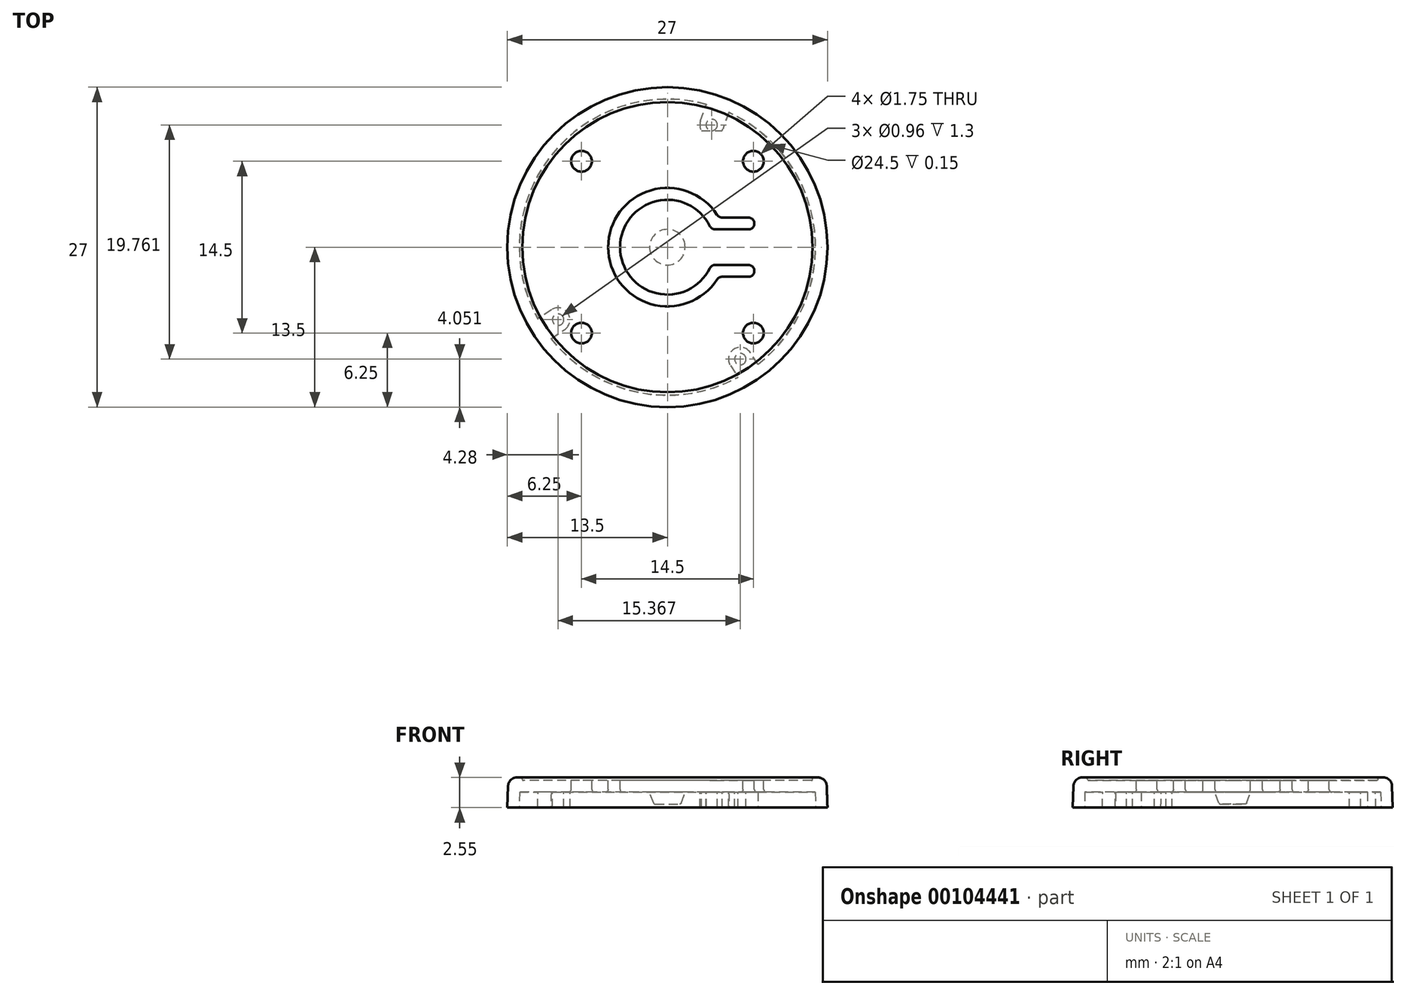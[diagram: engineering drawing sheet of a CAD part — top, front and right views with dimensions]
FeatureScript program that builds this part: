
annotation { "Feature Type Name" : "Feature", "Feature Type Description" : "" }
export const myFeature = defineFeature(function(context is Context, id is Id, definition is map)
    precondition{}
    {
        {
            var Q0;
            Q0=qCreatedBy(makeId("Top.planeOp"),FACE);
            var sketch = newSketch(context, id + "F0", { "sketchPlane" : qUnion([Q0])});
            skCircle(sketch, "E0", {"center": v(0, 0) * mm, "radius": 12.5 * mm});
            skCircle(sketch, "E1.0", {"center": v(0, 0) * mm, "radius": 13.5 * mm});
            skSolve(sketch);
        }
        {
            var Q0;
            Q0=qSketchRegion(id+"F0",true);
            var Q1;
            Q1=makeQuery(id+"F0.imprint","IMPRINT",FACE,{"disambiguationData":[TD([[makeQuery(id+"F0.imprint","IMPRINT",EDGE,{"derivedFrom":sQuery(id+"F0.wireOp",EDGE,"E0")}),1.0]])]});
            extrude(context, id + "F1", {"entities" : qUnion([Q0, Q1]), "depth" : 2.55 * mm, "hasDraft" : true, "draftAngle" : 2 * degree, "draftPullDirection" : true});
        }
        {
            var Q0;
            Q0=makeQuery(id+"F0.imprint","IMPRINT",FACE,{"disambiguationData":[TD([[makeQuery(id+"F0.imprint","IMPRINT",EDGE,{"derivedFrom":sQuery(id+"F0.wireOp",EDGE,"E0")}),1.0]])]});
            extrude(context, id + "F2", {"entities" : qUnion([Q0]), "operationType" : NewBodyOperationType.REMOVE, "depth" : 1.3 * mm, "hasDraft" : true, "draftAngle" : 1 * degree, "draftPullDirection" : true});
        }
        {
            var Q0;
            Q0=makeQuery(id+"F1.opExtrude","CAP_EDGE",EDGE,{"disambiguationData":[OSD([sQuery(id+"F0.wireOp",EDGE,"E1.0")])],"isStart":false});
            fillet(context, id + "F3", {"entities" : qUnion([Q0]), "radius" : .75 * mm, "tangentPropagation" : true, "allowEdgeOverflow" : false});
        }
        {
            var Q0;
            Q0=makeQuery(id+"F1.opExtrude","CAP_FACE",FACE,{"disambiguationData":[OSD([sQuery(id+"F0.wireOp",EDGE,"E1.0")])],"isStart":false});
            var sketch = newSketch(context, id + "F4", { "sketchPlane" : qUnion([Q0])});
            skCircle(sketch, "E2", {"center": v(0, 0) * mm, "radius": 12.25 * mm});
            skSolve(sketch);
        }
        {
            var Q0;
            Q0=qSketchRegion(id+"F4",true);
            extrude(context, id + "F5", {"entities" : qUnion([Q0]), "operationType" : NewBodyOperationType.REMOVE, "oppositeDirection" : true, "depth" : .25 * mm});
        }
        {
            var Q0;
            Q0=makeQuery(id+"F5.boolean.opBoolean","COPY",EDGE,{"derivedFrom":makeQuery(id+"F5.opExtrude","CAP_EDGE",EDGE,{"disambiguationData":[OSD([sQuery(id+"F4.wireOp",EDGE,"E2")])],"isStart":false})});
            var Q1;
            Q1=makeQuery(id+"F5.boolean.opBoolean","COPY",EDGE,{"derivedFrom":makeQuery(id+"F5.opExtrude","CAP_EDGE",EDGE,{"disambiguationData":[OSD([sQuery(id+"F4.wireOp",EDGE,"E2")])],"isStart":true})});
            fillet(context, id + "F6", {"entities" : qUnion([Q0, Q1]), "radius" : .1 * mm, "tangentPropagation" : true, "allowEdgeOverflow" : false});
        }
        {
            var Q0;
            Q0=makeQuery(id+"F5.boolean.opBoolean","COPY",FACE,{"derivedFrom":makeQuery(id+"F5.opExtrude","CAP_FACE",FACE,{"disambiguationData":[OSD([sQuery(id+"F4.wireOp",EDGE,"E2")])],"isStart":false})});
            var sketch = newSketch(context, id + "F7", { "sketchPlane" : qUnion([Q0])});
            skArc(sketch, "E3", {"start": v(3.58, 1.78) * mm, "mid": v(-4, 0) * mm, "end": v(3.58, -1.78) * mm});
            skLineSegment(sketch, "E4", {"start": v(0, 0) * mm, "end": v(11.07, 0) * mm, "construction": true});
            skLineSegment(sketch, "E5", {"start": v(4.03, 1.5) * mm, "end": v(6.83, 1.5) * mm});
            skLineSegment(sketch, "E6", {"start": v(7.33, 2) * mm, "end": v(7.33, 2) * mm});
            skLineSegment(sketch, "E7", {"start": v(6.83, 2.5) * mm, "end": v(4.6, 2.5) * mm});
            skLineSegment(sketch, "E8.0.MirrorCS", {"start": v(4.03, -1.5) * mm, "end": v(6.83, -1.5) * mm});
            skLineSegment(sketch, "E8.1.MirrorCS", {"start": v(6.83, -2.5) * mm, "end": v(4.6, -2.5) * mm});
            skLineSegment(sketch, "E8.2.MirrorCS", {"start": v(7.33, -2) * mm, "end": v(7.33, -2) * mm});
            skArc(sketch, "E9.trimOffspring", {"start": v(4.2, 2.73) * mm, "mid": v(-5, 0) * mm, "end": v(4.2, -2.73) * mm});
            skPoint(sketch, "E10.visualSharp", {"position": v(3.7, 1.5) * mm});
            skArc(sketch, "E10.filletArc", {"start": v(3.58, 1.78) * mm, "mid": v(3.77, 1.58) * mm, "end": v(4.03, 1.5) * mm});
            skPoint(sketch, "E11.visualSharp", {"position": v(4.33, 2.5) * mm});
            skArc(sketch, "E11.filletArc", {"start": v(4.2, 2.73) * mm, "mid": v(4.37, 2.56) * mm, "end": v(4.6, 2.5) * mm});
            skPoint(sketch, "E12.visualSharp", {"position": v(7.33, 2.5) * mm});
            skArc(sketch, "E12.filletArc", {"start": v(7.33, 2) * mm, "mid": v(7.18, 2.35) * mm, "end": v(6.83, 2.5) * mm});
            skPoint(sketch, "E13.visualSharp", {"position": v(7.33, 1.5) * mm});
            skArc(sketch, "E13.filletArc", {"start": v(6.83, 1.5) * mm, "mid": v(7.18, 1.65) * mm, "end": v(7.33, 2) * mm});
            skPoint(sketch, "E14.visualSharp", {"position": v(7.33, -1.5) * mm});
            skArc(sketch, "E14.filletArc", {"start": v(7.33, -2) * mm, "mid": v(7.18, -1.65) * mm, "end": v(6.83, -1.5) * mm});
            skPoint(sketch, "E15.visualSharp", {"position": v(7.33, -2.5) * mm});
            skArc(sketch, "E15.filletArc", {"start": v(6.83, -2.5) * mm, "mid": v(7.18, -2.35) * mm, "end": v(7.33, -2) * mm});
            skPoint(sketch, "E16.visualSharp", {"position": v(4.33, -2.5) * mm});
            skArc(sketch, "E16.filletArc", {"start": v(4.6, -2.5) * mm, "mid": v(4.37, -2.56) * mm, "end": v(4.2, -2.73) * mm});
            skPoint(sketch, "E17.visualSharp", {"position": v(3.7, -1.5) * mm});
            skArc(sketch, "E17.filletArc", {"start": v(4.03, -1.5) * mm, "mid": v(3.77, -1.58) * mm, "end": v(3.58, -1.78) * mm});
            skSolve(sketch);
        }
        {
            var Q0;
            Q0=qSketchRegion(id+"F7",true);
            extrude(context, id + "F8", {"entities" : qUnion([Q0]), "operationType" : NewBodyOperationType.REMOVE, "endBound" : BoundingType.THROUGH_ALL, "oppositeDirection" : true, "depth" : 25 * mm});
        }
        {
            var Q0;
            Q0=makeQuery(id+"F8.boolean.opBoolean","COPY",EDGE,{"derivedFrom":makeQuery(id+"F8.opExtrude","CAP_EDGE",EDGE,{"disambiguationData":[OSD([sQuery(id+"F7.wireOp",EDGE,"E9.trimOffspring")])],"isStart":true})});
            var Q1;
            Q1=makeQuery(id+"F8.boolean.opBoolean","INTERSECT",EDGE,{"derivedFrom":[makeQuery(id+"F2.boolean.opBoolean","COPY",FACE,{"derivedFrom":makeQuery(id+"F2.opExtrude","CAP_FACE",FACE,{"disambiguationData":[OSD([sQuery(id+"F0.wireOp",EDGE,"E0")])],"isStart":false})}),makeQuery(id+"F8.opExtrude","SWEPT_FACE",FACE,{"disambiguationData":[OSD([sQuery(id+"F7.wireOp",EDGE,"E9.trimOffspring")])]})]});
            fillet(context, id + "F9", {"entities" : qUnion([Q0, Q1]), "radius" : .25 * mm, "tangentPropagation" : true, "allowEdgeOverflow" : false});
        }
        {
            var Q0;
            Q0=makeQuery(id+"F2.boolean.opBoolean","COPY",FACE,{"derivedFrom":makeQuery(id+"F2.opExtrude","CAP_FACE",FACE,{"disambiguationData":[OSD([sQuery(id+"F0.wireOp",EDGE,"E0")])],"isStart":false})});
            var sketch = newSketch(context, id + "F10", { "sketchPlane" : qUnion([Q0])});
            skCircle(sketch, "E18", {"center": v(0, 0) * mm, "radius": 1.5 * mm});
            skSolve(sketch);
        }
        {
            var Q0;
            Q0=qSketchRegion(id+"F10",true);
            extrude(context, id + "F11", {"entities" : qUnion([Q0]), "operationType" : NewBodyOperationType.ADD, "depth" : 1 * mm, "hasDraft" : true, "draftAngle" : 20 * degree, "draftPullDirection" : true});
        }
        {
            var Q0;
            Q0=makeQuery(id+"F11.opExtrude","CAP_EDGE",EDGE,{"disambiguationData":[OSD([sQuery(id+"F10.wireOp",EDGE,"E18")])],"isStart":false});
            var Q1;
            Q1=makeQuery(id+"F11.opExtrude","CAP_EDGE",EDGE,{"disambiguationData":[OSD([sQuery(id+"F10.wireOp",EDGE,"E18")])],"isStart":true});
            fillet(context, id + "F12", {"entities" : qUnion([Q0, Q1]), "radius" : .15 * mm, "tangentPropagation" : true, "allowEdgeOverflow" : false});
        }
        {
            var Q0;
            Q0=makeQuery(id+"F5.boolean.opBoolean","COPY",FACE,{"derivedFrom":makeQuery(id+"F5.opExtrude","CAP_FACE",FACE,{"disambiguationData":[OSD([sQuery(id+"F4.wireOp",EDGE,"E2")])],"isStart":false})});
            var sketch = newSketch(context, id + "F13", { "sketchPlane" : qUnion([Q0])});
            skPoint(sketch, "E19.center", {"position": v(0, 0) * mm});
            skLineSegment(sketch, "E20", {"start": v(0, 0) * mm, "end": v(0, 14.83) * mm, "construction": true});
            skCircle(sketch, "E21", {"center": v(-7.25, 7.25) * mm, "radius": 0.88 * mm});
            skCircle(sketch, "E22.1.0", {"center": v(-7.25, -7.25) * mm, "radius": 0.88 * mm});
            skCircle(sketch, "E22.2.0", {"center": v(7.25, -7.25) * mm, "radius": 0.88 * mm});
            skCircle(sketch, "E22.3.0", {"center": v(7.25, 7.25) * mm, "radius": 0.88 * mm});
            skSolve(sketch);
        }
        {
            var Q0;
            Q0=qSketchRegion(id+"F13",true);
            extrude(context, id + "F14", {"entities" : qUnion([Q0]), "operationType" : NewBodyOperationType.REMOVE, "endBound" : BoundingType.THROUGH_ALL, "oppositeDirection" : true, "depth" : 25 * mm});
        }
        {
            var Q0;
            Q0=makeQuery(id+"F14.boolean.opBoolean","COPY",EDGE,{"derivedFrom":makeQuery(id+"F14.opExtrude","CAP_EDGE",EDGE,{"disambiguationData":[OSD([sQuery(id+"F13.wireOp",EDGE,"E21")])],"isStart":true})});
            var Q1;
            Q1=makeQuery(id+"F14.boolean.opBoolean","COPY",EDGE,{"derivedFrom":makeQuery(id+"F14.opExtrude","CAP_EDGE",EDGE,{"disambiguationData":[OSD([sQuery(id+"F13.wireOp",EDGE,"E22.3.0")])],"isStart":true})});
            var Q2;
            Q2=makeQuery(id+"F14.boolean.opBoolean","COPY",EDGE,{"derivedFrom":makeQuery(id+"F14.opExtrude","CAP_EDGE",EDGE,{"disambiguationData":[OSD([sQuery(id+"F13.wireOp",EDGE,"E22.2.0")])],"isStart":true})});
            var Q3;
            Q3=makeQuery(id+"F14.boolean.opBoolean","COPY",EDGE,{"derivedFrom":makeQuery(id+"F14.opExtrude","CAP_EDGE",EDGE,{"disambiguationData":[OSD([sQuery(id+"F13.wireOp",EDGE,"E22.1.0")])],"isStart":true})});
            var Q4;
            Q4=makeQuery(id+"F14.boolean.opBoolean","INTERSECT",EDGE,{"derivedFrom":[makeQuery(id+"F2.boolean.opBoolean","COPY",FACE,{"derivedFrom":makeQuery(id+"F2.opExtrude","CAP_FACE",FACE,{"disambiguationData":[OSD([sQuery(id+"F0.wireOp",EDGE,"E0")])],"isStart":false})}),makeQuery(id+"F14.opExtrude","SWEPT_FACE",FACE,{"disambiguationData":[OSD([sQuery(id+"F13.wireOp",EDGE,"E22.1.0")])]})]});
            var Q5;
            Q5=makeQuery(id+"F14.boolean.opBoolean","INTERSECT",EDGE,{"derivedFrom":[makeQuery(id+"F2.boolean.opBoolean","COPY",FACE,{"derivedFrom":makeQuery(id+"F2.opExtrude","CAP_FACE",FACE,{"disambiguationData":[OSD([sQuery(id+"F0.wireOp",EDGE,"E0")])],"isStart":false})}),makeQuery(id+"F14.opExtrude","SWEPT_FACE",FACE,{"disambiguationData":[OSD([sQuery(id+"F13.wireOp",EDGE,"E21")])]})]});
            var Q6;
            Q6=makeQuery(id+"F14.boolean.opBoolean","INTERSECT",EDGE,{"derivedFrom":[makeQuery(id+"F2.boolean.opBoolean","COPY",FACE,{"derivedFrom":makeQuery(id+"F2.opExtrude","CAP_FACE",FACE,{"disambiguationData":[OSD([sQuery(id+"F0.wireOp",EDGE,"E0")])],"isStart":false})}),makeQuery(id+"F14.opExtrude","SWEPT_FACE",FACE,{"disambiguationData":[OSD([sQuery(id+"F13.wireOp",EDGE,"E22.3.0")])]})]});
            var Q7;
            Q7=makeQuery(id+"F14.boolean.opBoolean","INTERSECT",EDGE,{"derivedFrom":[makeQuery(id+"F2.boolean.opBoolean","COPY",FACE,{"derivedFrom":makeQuery(id+"F2.opExtrude","CAP_FACE",FACE,{"disambiguationData":[OSD([sQuery(id+"F0.wireOp",EDGE,"E0")])],"isStart":false})}),makeQuery(id+"F14.opExtrude","SWEPT_FACE",FACE,{"disambiguationData":[OSD([sQuery(id+"F13.wireOp",EDGE,"E22.2.0")])]})]});
            fillet(context, id + "F15", {"entities" : qUnion([Q0, Q1, Q2, Q3, Q4, Q5, Q6, Q7]), "radius" : .25 * mm, "tangentPropagation" : true, "allowEdgeOverflow" : false});
        }
        {
            var Q0;
            Q0=makeQuery(id+"F2.boolean.opBoolean","COPY",FACE,{"derivedFrom":makeQuery(id+"F2.opExtrude","CAP_FACE",FACE,{"disambiguationData":[OSD([sQuery(id+"F0.wireOp",EDGE,"E0")])],"isStart":false})});
            var sketch = newSketch(context, id + "F16", { "sketchPlane" : qUnion([Q0])});
            skLineSegment(sketch, "E23", {"start": v(0, 0) * mm, "end": v(6.15, 9.45) * mm, "construction": true});
            skLineSegment(sketch, "E24", {"start": v(0, 0) * mm, "end": v(18.94, 0) * mm, "construction": true});
            skCircle(sketch, "E25", {"center": v(6.15, 9.45) * mm, "radius": 1 * mm});
            skLineSegment(sketch, "E26", {"start": v(0, 0) * mm, "end": v(3.73, -10.31) * mm, "construction": true});
            skCircle(sketch, "E27", {"center": v(3.73, -10.31) * mm, "radius": 1 * mm});
            skLineSegment(sketch, "E28", {"start": v(0, 0) * mm, "end": v(-9.22, 6.12) * mm, "construction": true});
            skCircle(sketch, "E29", {"center": v(-9.22, 6.12) * mm, "radius": 1 * mm});
            skLineSegment(sketch, "E30", {"start": v(2.86, -9.83) * mm, "end": v(4.6, -9.83) * mm});
            skCircle(sketch, "E31", {"center": v(3.73, -10.31) * mm, "radius": 0.48 * mm});
            skCircle(sketch, "E32", {"center": v(-9.22, 6.12) * mm, "radius": 0.48 * mm});
            skCircle(sketch, "E33", {"center": v(6.15, 9.45) * mm, "radius": 0.48 * mm});
            skLineSegment(sketch, "E34", {"start": v(-9.77, 5.29) * mm, "end": v(-11.47, 6.42) * mm});
            skLineSegment(sketch, "E35", {"start": v(-11.47, 6.42) * mm, "end": v(-10.36, 8.08) * mm});
            skLineSegment(sketch, "E36", {"start": v(-10.36, 8.08) * mm, "end": v(-8.67, 6.95) * mm});
            skLineSegment(sketch, "E37", {"start": v(2.8, -10.65) * mm, "end": v(3.45, -12.48) * mm});
            skLineSegment(sketch, "E38", {"start": v(3.45, -12.48) * mm, "end": v(5.32, -11.75) * mm});
            skLineSegment(sketch, "E39", {"start": v(5.32, -11.75) * mm, "end": v(4.67, -9.97) * mm});
            skLineSegment(sketch, "E40", {"start": v(5.3, 10) * mm, "end": v(6.23, 11.41) * mm});
            skLineSegment(sketch, "E41", {"start": v(6.23, 11.41) * mm, "end": v(7.9, 10.32) * mm});
            skLineSegment(sketch, "E42", {"start": v(7.9, 10.32) * mm, "end": v(6.98, 8.9) * mm});
            skSolve(sketch);
        }
        {
            var Q0;
            {var subQ3=sQuery(id+"F16.wireOp",EDGE,"E35");Q0=makeQuery(id+"F16.imprint","IMPRINT",FACE,{"disambiguationData":[TD([[makeQuery(id+"F16.imprint","IMPRINT",EDGE,{"derivedFrom":subQ3}),-1.0]])]});}
            var Q1;
            Q1=makeQuery(id+"F16.imprint","IMPRINT",FACE,{"disambiguationData":[TD([[makeQuery(id+"F16.imprint","IMPRINT",EDGE,{"derivedFrom":sQuery(id+"F16.wireOp",EDGE,"E32")}),-1.0]])]});
            var Q2;
            {var subQ0=sQuery(id+"F16.wireOp",EDGE,"E34");var subQ3=sQuery(id+"F16.wireOp",EDGE,"E29");var subQ4=makeQuery(id+"F16.imprint","INTERSECT",VERTEX,{"derivedFrom":[subQ3,subQ0]});Q2=makeQuery(id+"F16.imprint","IMPRINT",FACE,{"disambiguationData":[TD([[makeQuery(id+"F16.imprint","IMPRINT",EDGE,{"disambiguationData":[TD([[subQ4,1.0]])],"derivedFrom":subQ3}),-1.0]])]});}
            var Q3;
            Q3=makeQuery(id+"F16.imprint","IMPRINT",FACE,{"disambiguationData":[TD([[makeQuery(id+"F16.imprint","IMPRINT",EDGE,{"derivedFrom":sQuery(id+"F16.wireOp",EDGE,"E33")}),-1.0]])]});
            var Q4;
            {var subQ3=sQuery(id+"F16.wireOp",EDGE,"E40");var subQ5=sQuery(id+"F16.wireOp",EDGE,"E25");var subQ7=makeQuery(id+"F16.imprint","INTERSECT",VERTEX,{"derivedFrom":[subQ5,subQ3]});Q4=makeQuery(id+"F16.imprint","IMPRINT",FACE,{"disambiguationData":[TD([[makeQuery(id+"F16.imprint","IMPRINT",EDGE,{"disambiguationData":[TD([[subQ7,1.0]])],"derivedFrom":subQ5}),-1.0]])]});}
            var Q5;
            {var subQ3=sQuery(id+"F16.wireOp",EDGE,"E41");Q5=makeQuery(id+"F16.imprint","IMPRINT",FACE,{"disambiguationData":[TD([[makeQuery(id+"F16.imprint","IMPRINT",EDGE,{"derivedFrom":subQ3}),-1.0]])]});}
            var Q6;
            {var subQ5=sQuery(id+"F16.wireOp",EDGE,"E38");Q6=makeQuery(id+"F16.imprint","IMPRINT",FACE,{"disambiguationData":[TD([[makeQuery(id+"F16.imprint","IMPRINT",EDGE,{"derivedFrom":subQ5}),1.0]])]});}
            var Q7;
            {var subQ3=sQuery(id+"F16.wireOp",EDGE,"E27");var subQ5=sQuery(id+"F16.wireOp",EDGE,"E37");var subQ7=makeQuery(id+"F16.imprint","INTERSECT",VERTEX,{"derivedFrom":[subQ3,subQ5]});Q7=makeQuery(id+"F16.imprint","IMPRINT",FACE,{"disambiguationData":[TD([[makeQuery(id+"F16.imprint","IMPRINT",EDGE,{"disambiguationData":[TD([[subQ7,-1.0]])],"derivedFrom":subQ3}),-1.0]])]});}
            var Q8;
            {var subQ2=sQuery(id+"F16.wireOp",EDGE,"E30");Q8=makeQuery(id+"F16.imprint","IMPRINT",FACE,{"disambiguationData":[TD([[makeQuery(id+"F16.imprint","IMPRINT",EDGE,{"derivedFrom":subQ2}),-1.0]])]});}
            extrude(context, id + "F17", {"entities" : qUnion([Q0, Q1, Q2, Q3, Q4, Q5, Q6, Q7, Q8]), "operationType" : NewBodyOperationType.ADD, "depth" : 1.3 * mm});
        }
    });
